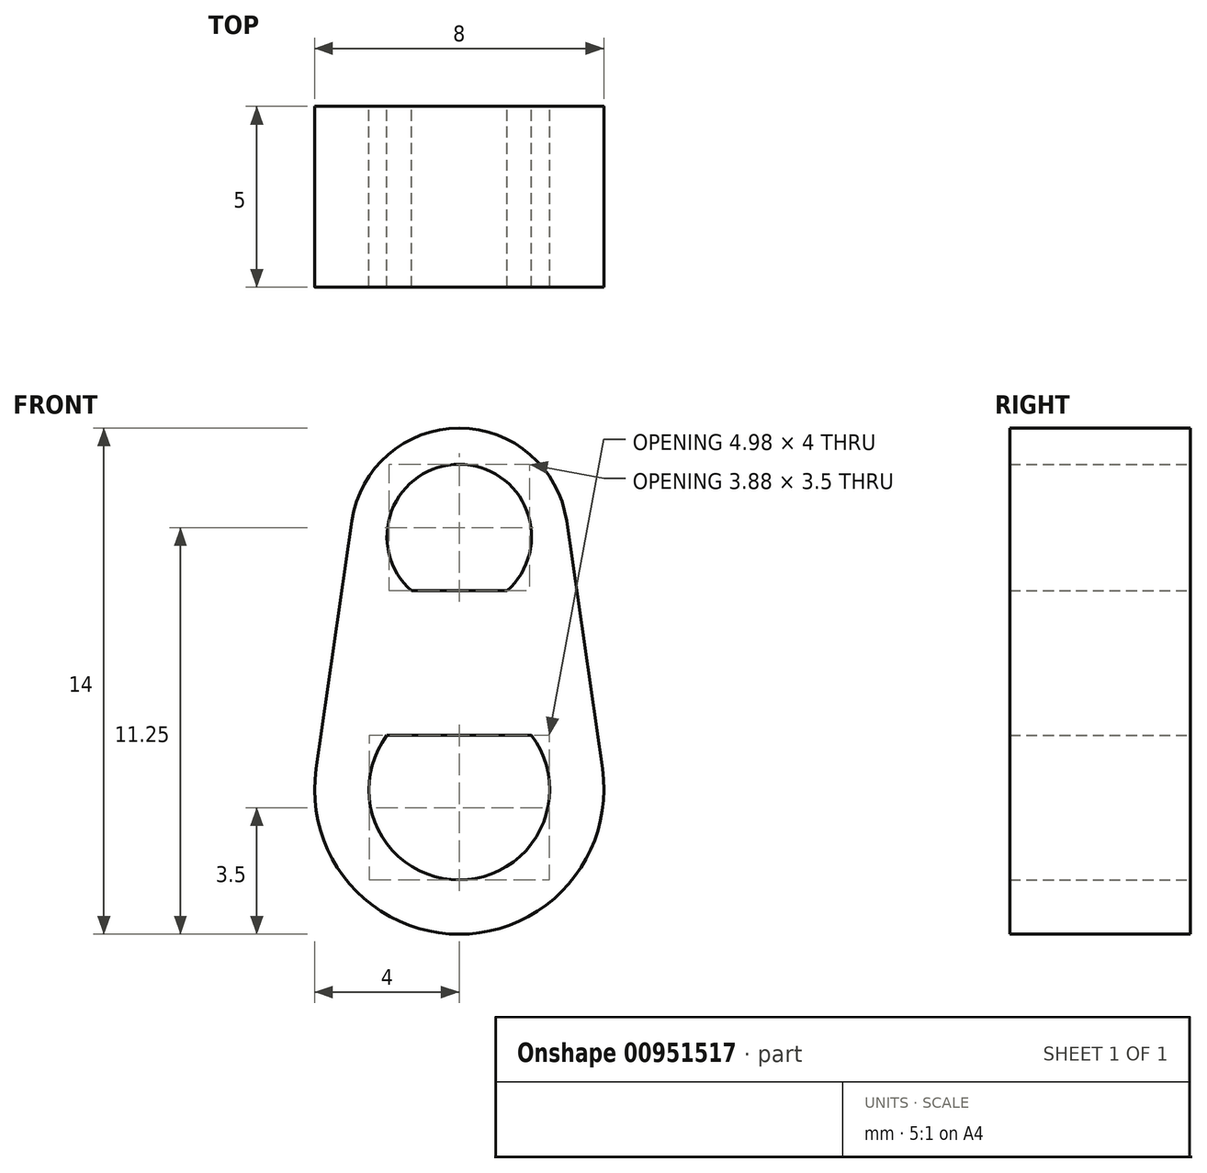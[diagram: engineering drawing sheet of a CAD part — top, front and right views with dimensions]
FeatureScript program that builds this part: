
annotation { "Feature Type Name" : "Feature", "Feature Type Description" : "" }
export const myFeature = defineFeature(function(context is Context, id is Id, definition is map)
    precondition{}
    {
        {
            var Q0;
            Q0=qCreatedBy(makeId("Front.planeOp"),FACE);
            var sketch = newSketch(context, id + "F0", { "sketchPlane" : qUnion([Q0])});
            skCircle(sketch, "E0", {"center": v(0, 0) * mm, "radius": 2 * mm});
            skCircle(sketch, "E1", {"center": v(0, -7) * mm, "radius": 2.5 * mm});
            skCircle(sketch, "E2", {"center": v(0, 0) * mm, "radius": 3 * mm});
            skCircle(sketch, "E3", {"center": v(0, -7) * mm, "radius": 4 * mm});
            skLineSegment(sketch, "E4", {"start": v(-2.97, 0.43) * mm, "end": v(-3.96, -6.43) * mm});
            skLineSegment(sketch, "E5", {"start": v(2.97, 0.43) * mm, "end": v(3.96, -6.43) * mm});
            skLineSegment(sketch, "E6", {"start": v(1.32, -1.5) * mm, "end": v(-1.32, -1.5) * mm});
            skLineSegment(sketch, "E7", {"start": v(-2, -5.5) * mm, "end": v(2, -5.5) * mm});
            skSolve(sketch);
        }
        {
            var Q0;
            Q0 = qSketchRegion(id + "F0", true);
            var Q1;
            {var subQ0=sQuery(id+"F0.wireOp",EDGE,"E7");Q1=makeQuery(id+"F0.imprint","IMPRINT",FACE,{"disambiguationData":[TD([[makeQuery(id+"F0.imprint","IMPRINT",EDGE,{"derivedFrom":subQ0}),1.0]])]});}
            var Q2;
            {var subQ0=sQuery(id+"F0.wireOp",EDGE,"E6");Q2=makeQuery(id+"F0.imprint","IMPRINT",FACE,{"disambiguationData":[TD([[makeQuery(id+"F0.imprint","IMPRINT",EDGE,{"derivedFrom":subQ0}),1.0]])]});}
            extrude(context, id + "F1", {"entities" : qUnion([Q0, Q1, Q2]), "depth" : 5 * mm, "offsetDistance" : 25 * mm});
        }
    });
